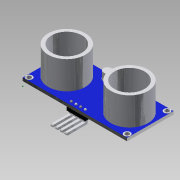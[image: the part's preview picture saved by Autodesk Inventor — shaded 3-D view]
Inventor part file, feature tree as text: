
AUTODESK INVENTOR PART (.ipt)
format: ipt  version: 2016 (Build 200138000, 138)  size: 407,552 bytes
history: native  units: mm
features: sketch x21, projected_geometry x16, extrude x15, revolve x4
ambient origin geometry x8: Origin, YZ Plane, XZ Plane, XY Plane, X Axis, Y Axis, Z Axis, Center Point
bodies: Solid1 (feature_tree)
feature tree (56):
  extrude  "Extrusion1"  Depth=20.0mm
  extrude  "Extrusion2"  Depth=7.0mm TaperAngle=0.0deg
  extrude  "Extrusion3"  Depth=7.0mm TaperAngle=0.0deg
  extrude  "Extrusion4"  Depth=13.0mm
  extrude  "Extrusion5"  Depth=5.0mm TaperAngle=0.0deg
  extrude  "Extrusion6"  Depth=0.2mm TaperAngle=0.0deg
  extrude  "Extrusion7"  Depth=3.0mm
  extrude  "Extrusion8"  Depth=2.0mm
  extrude  "Extrusion9"  Depth=0.1mm TaperAngle=0.0deg
  extrude  "Extrusion10"  Depth=0.1mm TaperAngle=0.0deg
  extrude  "Extrusion11"  TaperAngle=90.0deg  [1 undecoded]
  revolve  "Revolution1"  Angle=180.0deg
  revolve  "Revolution2"  [1 undecoded]
  revolve  "Revolution3"  [1 undecoded]
  revolve  "Revolution4"  [1 undecoded]
  extrude  "Extrusion12"  Depth=8.0mm TaperAngle=0.0deg
  sketch  "Sketch17"  dims[d68=0.5mm d69=0.5mm]
  sketch  "Sketch18"  dims[d70=80.0mm d71=0.0mm]
  extrude  "Extrusion13"  Depth=0.5mm
  extrude  "Extrusion14"  [1 undecoded]
  extrude  "Extrusion15"  [1 undecoded]
  sketch  "Sketch1"  dims[d0=45.0mm d1=20.0mm]
  sketch  "Sketch2"  dims[d2=1.3mm d3=0.0mm d6=7.0mm d7=0.0mm]
  sketch  "Sketch3"  dims[d13=7.0mm d14=0.0mm d19=7.0mm d20=0.0mm]
  sketch  "Sketch4"  dims[d21=13.0mm d22=13.0mm]
  sketch  "Sketch5"  dims[d23=10.0mm d24=0.0mm d25=5.0mm d26=0.0mm]
  projected_geometry  "Projected Loop1"
  projected_geometry  "Projected Loop2"
  sketch  "Sketch6"  dims[d27=1.0mm d28=0.0mm d36=0.2mm d37=0.0mm]
  projected_geometry  "Projected Loop3"
  projected_geometry  "Projected Loop4"
  sketch  "Sketch7"  dims[d42=3.0mm d43=0.0mm d44=2.7mm]
  projected_geometry  "Projected Loop5"
  sketch  "Sketch8"  dims[d45=2.7mm d46=2.0mm]
  projected_geometry  "Projected Loop6"
  sketch  "Sketch9"  dims[d47=2.7mm d48=0.1mm d49=0.0mm]
  projected_geometry  "Projected Loop7"
  sketch  "Sketch10"  dims[d50=2.7mm d51=0.1mm d52=0.0mm]
  projected_geometry  "Projected Loop8"
  sketch  "Sketch11"  dims[d53=90.0deg d54=90.0deg]
  sketch  "Sketch12"  dims[d55=180.0deg d56=180.0deg]
  projected_geometry  "Projected Loop9"
  sketch  "Sketch13"  dims[d57=180.0deg d58=2.0mm]
  projected_geometry  "Projected Loop10"
  sketch  "Sketch14"  dims[d59=2.0mm d60=2.0mm]
  sketch  "Sketch15"  dims[d61=2.0mm d62=2.0mm d63=0.0mm]
  sketch  "Sketch16"  dims[d64=2.0mm d65=0.0mm d66=8.0mm d67=0.0mm]
  projected_geometry  "Projected Loop11"
  sketch  "Sketch19"
  projected_geometry  "Projected Loop12"
  sketch  "Sketch20"
  projected_geometry  "Projected Loop13"
  projected_geometry  "Projected Loop14"
  projected_geometry  "Projected Loop15"
  sketch  "Sketch21"
  projected_geometry  "Projected Loop16"
note: 6 required parameter values undecoded (feature->parameter linkage not recoverable at this tier; creation-order binding heuristic only, values carry confidence <= 0.55)